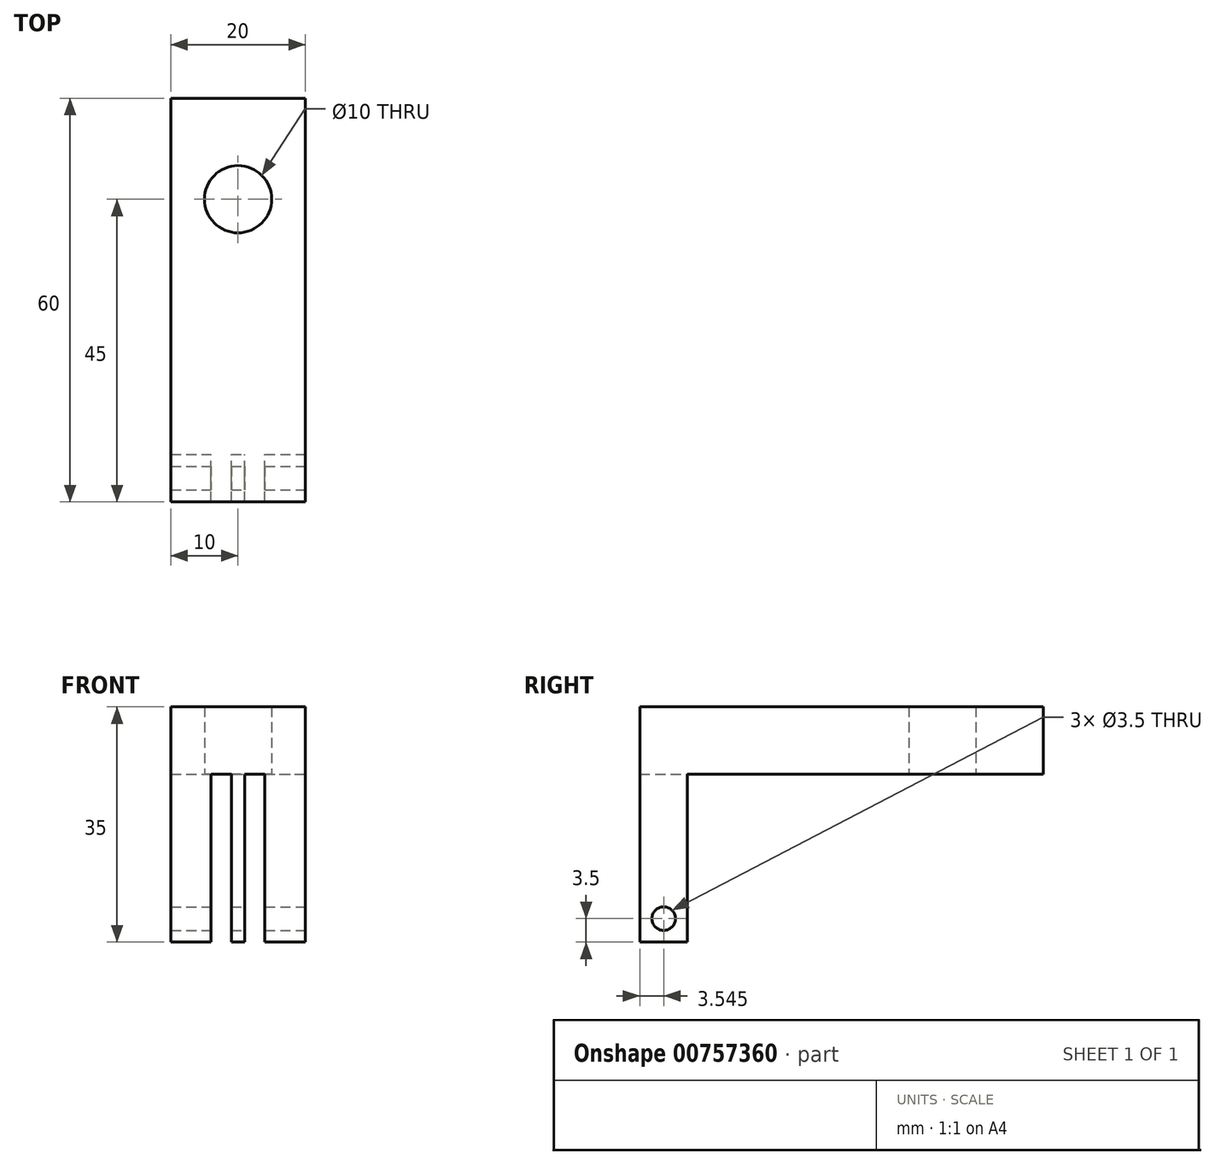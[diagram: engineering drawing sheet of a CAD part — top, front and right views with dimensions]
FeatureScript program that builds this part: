
annotation { "Feature Type Name" : "Feature", "Feature Type Description" : "" }
export const myFeature = defineFeature(function(context is Context, id is Id, definition is map)
    precondition{}
    {
        {
            var Q0;
            Q0=qCreatedBy(makeId("Top.planeOp"),FACE);
            var sketch = newSketch(context, id + "F0", { "sketchPlane" : qUnion([Q0])});
            skLineSegment(sketch, "E0.bottom", {"start": v(-10, 14.13) * mm, "end": v(10, 14.13) * mm});
            skLineSegment(sketch, "E0.top", {"start": v(-10, -45.87) * mm, "end": v(10, -45.87) * mm});
            skLineSegment(sketch, "E0.left", {"start": v(-10, 14.13) * mm, "end": v(-10, -45.87) * mm});
            skLineSegment(sketch, "E0.right", {"start": v(10, 14.13) * mm, "end": v(10, -45.87) * mm});
            skCircle(sketch, "E1", {"center": v(0, -0.87) * mm, "radius": 5 * mm});
            skSolve(sketch);
        }
        {
            var Q0;
            Q0 = qSketchRegion(id + "F0", true);
            extrude(context, id + "F1", {"entities" : qUnion([Q0]), "depth" : 10 * mm, "offsetDistance" : 25 * mm});
        }
        {
            var Q0;
            Q0=makeQuery(id+"F1.opExtrude","CAP_FACE",FACE,{"disambiguationData":[OSD([sQuery(id+"F0.wireOp",EDGE,"E0.bottom"),sQuery(id+"F0.wireOp",EDGE,"E0.top"),sQuery(id+"F0.wireOp",EDGE,"E0.left"),sQuery(id+"F0.wireOp",EDGE,"E0.right"),sQuery(id+"F0.wireOp",EDGE,"E1")])],"isStart":true});
            var sketch = newSketch(context, id + "F2", { "sketchPlane" : qUnion([Q0])});
            skLineSegment(sketch, "E2.bottom", {"start": v(-1, 45.87) * mm, "end": v(1, 45.87) * mm});
            skLineSegment(sketch, "E2.top", {"start": v(-1, 38.82) * mm, "end": v(1, 38.82) * mm});
            skLineSegment(sketch, "E2.left", {"start": v(-1, 45.87) * mm, "end": v(-1, 38.82) * mm});
            skLineSegment(sketch, "E2.right", {"start": v(1, 45.87) * mm, "end": v(1, 38.82) * mm});
            skLineSegment(sketch, "E3.bottom", {"start": v(-10, 45.87) * mm, "end": v(-4, 45.87) * mm});
            skLineSegment(sketch, "E3.top", {"start": v(-10, 38.82) * mm, "end": v(-4, 38.82) * mm});
            skLineSegment(sketch, "E3.left", {"start": v(-10, 45.87) * mm, "end": v(-10, 38.82) * mm});
            skLineSegment(sketch, "E3.right", {"start": v(-4, 45.87) * mm, "end": v(-4, 38.82) * mm});
            skLineSegment(sketch, "E4.bottom", {"start": v(4, 45.87) * mm, "end": v(10, 45.87) * mm});
            skLineSegment(sketch, "E4.top", {"start": v(4, 38.82) * mm, "end": v(10, 38.82) * mm});
            skLineSegment(sketch, "E4.left", {"start": v(4, 45.87) * mm, "end": v(4, 38.82) * mm});
            skLineSegment(sketch, "E4.right", {"start": v(10, 45.87) * mm, "end": v(10, 38.82) * mm});
            skSolve(sketch);
        }
        {
            var Q0;
            Q0 = qSketchRegion(id + "F2", true);
            extrude(context, id + "F3", {"entities" : qUnion([Q0]), "operationType" : NewBodyOperationType.ADD, "depth" : 25 * mm, "offsetDistance" : 25 * mm});
        }
        {
            var Q0;
            Q0=makeQuery(id+"F3.boolean.opBoolean","MERGE",FACE,{"derivedFrom":[makeQuery(id+"F1.opExtrude","SWEPT_FACE",FACE,{"disambiguationData":[OSD([sQuery(id+"F0.wireOp",EDGE,"E0.right")])]}),makeQuery(id+"F3.opExtrude","SWEPT_FACE",FACE,{"disambiguationData":[OSD([sQuery(id+"F2.wireOp",EDGE,"E4.right")])]})]});
            var sketch = newSketch(context, id + "F4", { "sketchPlane" : qUnion([Q0])});
            skCircle(sketch, "E5", {"center": v(-42.32, -21.5) * mm, "radius": 1.75 * mm});
            skSolve(sketch);
        }
        {
            var Q0;
            Q0 = qSketchRegion(id + "F4", true);
            extrude(context, id + "F5", {"entities" : qUnion([Q0]), "operationType" : NewBodyOperationType.REMOVE, "oppositeDirection" : true, "depth" : 25 * mm, "offsetDistance" : 25 * mm});
        }
    });
